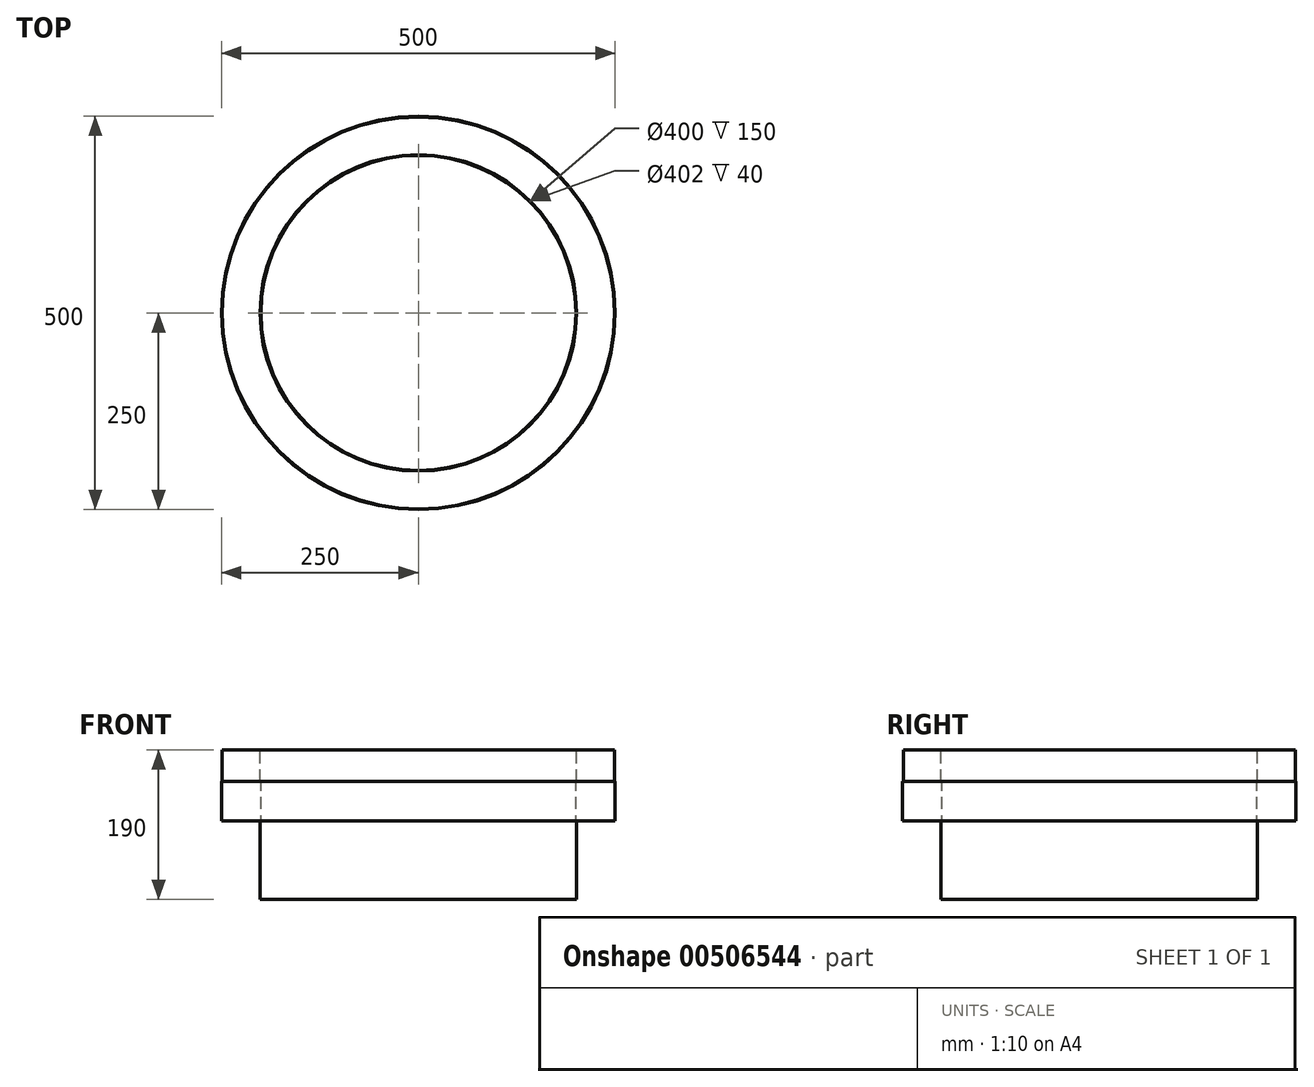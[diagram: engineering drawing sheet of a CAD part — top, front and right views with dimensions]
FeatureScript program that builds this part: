
annotation { "Feature Type Name" : "Feature", "Feature Type Description" : "" }
export const myFeature = defineFeature(function(context is Context, id is Id, definition is map)
    precondition{}
    {
        {
            var Q0;
            Q0=qCreatedBy(makeId("Front.planeOp"),FACE);
            var sketch = newSketch(context, id + "F0", { "sketchPlane" : qUnion([Q0])});
            skLineSegment(sketch, "E0", {"start": v(0, 710.75) * mm, "end": v(0, -704.58) * mm, "construction": true});
            skLineSegment(sketch, "E1", {"start": v(-200, 300.65) * mm, "end": v(-200, 410.65) * mm});
            skLineSegment(sketch, "E2", {"start": v(-200, 410.65) * mm, "end": v(-201, 410.65) * mm});
            skLineSegment(sketch, "E3", {"start": v(-249, 410.65) * mm, "end": v(-250, 410.65) * mm});
            skLineSegment(sketch, "E4", {"start": v(-250, 410.65) * mm, "end": v(-250, 360.65) * mm});
            skLineSegment(sketch, "E5", {"start": v(-250, 360.65) * mm, "end": v(-201, 360.65) * mm});
            skLineSegment(sketch, "E6", {"start": v(-201, 360.65) * mm, "end": v(-201, 300.65) * mm});
            skLineSegment(sketch, "E7", {"start": v(-249, 450.65) * mm, "end": v(-249, 410.65) * mm});
            skLineSegment(sketch, "E8", {"start": v(-249, 450.65) * mm, "end": v(-201, 450.65) * mm});
            skLineSegment(sketch, "E9", {"start": v(-201, 410.65) * mm, "end": v(-201, 450.65) * mm});
            skLineSegment(sketch, "E10", {"start": v(-200, 300.65) * mm, "end": v(-200, 260.65) * mm});
            skLineSegment(sketch, "E11", {"start": v(-201, 300.65) * mm, "end": v(-201, 260.65) * mm});
            skLineSegment(sketch, "E12", {"start": v(-201, 260.65) * mm, "end": v(-200, 260.65) * mm});
            skSolve(sketch);
        }
        {
            var Q0;
            Q0=qSketchRegion(id+"F0",true);
            var Q1;
            Q1=sQuery(id+"F0.wireOp",EDGE,"E0");
            revolve(context, id + "F1", {"entities" : qUnion([Q0]), "axis" : qUnion([Q1]), "revolveType" : RevolveType.FULL});
        }
    });
